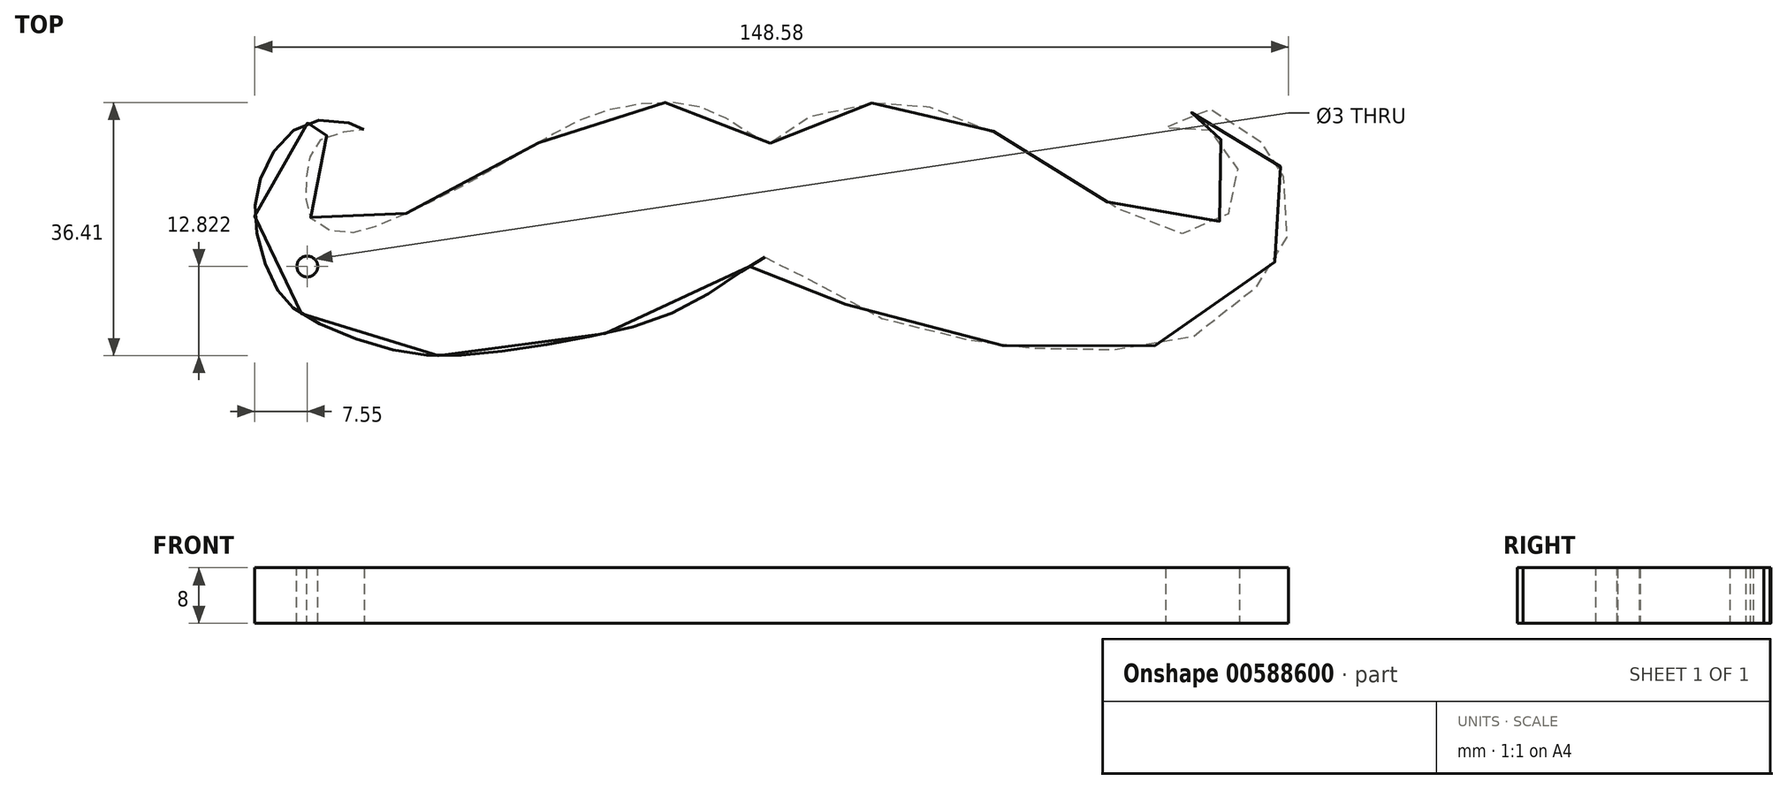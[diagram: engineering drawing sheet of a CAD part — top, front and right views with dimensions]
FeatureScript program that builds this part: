
annotation { "Feature Type Name" : "Feature", "Feature Type Description" : "" }
export const myFeature = defineFeature(function(context is Context, id is Id, definition is map)
    precondition{}
    {
        {
            var Q0;
            Q0=qCreatedBy(makeId("Top.planeOp"),FACE);
            var sketch = newSketch(context, id + "F0", { "sketchPlane" : qUnion([Q0])});
            skPoint(sketch, "E0.41.internal.snap0", {"position": v(0, 19.04) * mm});
            skPoint(sketch, "E0.42.internal.snap0", {"position": v(0, 19.04) * mm});
            skFitSpline(sketch, "E0", {"points": [v(-75.65, 31.5) * mm, v(-81.55, 34.82) * mm, v(-89.12, 37.31) * mm, v(-100.1, 35.93) * mm, v(-108.77, 31.69) * mm, v(-120.85, 24.86) * mm, v(-130.81, 20.15) * mm, v(-136.63, 18.59) * mm, v(-141.52, 20.52) * mm, v(-142.35, 24.86) * mm, v(-141.8, 29.56) * mm, v(-138.84, 32.8) * mm, v(-134.04, 33.53) * mm, v(-138.38, 34.82) * mm, v(-144.93, 32.8) * mm, v(-149.08, 25.87) * mm, v(-149.54, 19.14) * mm, v(-146.77, 10.93) * mm, v(-142.9, 6.87) * mm, v(-130.72, 1.98) * mm, v(-119.84, 1.06) * mm, v(-102.4, 3.55) * mm, v(-87.09, 8.35) * mm, v(-76.85, 14.9) * mm, v(-74.45, 15.08) * mm, v(-66.51, 9.27) * mm, v(-48.25, 3.46) * mm, v(-39.58, 2.16) * mm, v(-25.37, 1.89) * mm, v(-11.62, 5.4) * mm, v(-2.95, 14.71) * mm, v(-1.19, 19.62) * mm, v(-2.02, 27.42) * mm, v(-2.57, 28.46) * mm, v(-7.96, 34.54) * mm, v(-14.66, 36.06) * mm, v(-18.81, 33.78) * mm, v(-15.42, 34.4) * mm, v(-10.3, 31.36) * mm, v(-8.37, 27.22) * mm, v(-9, 22.45) * mm, v(-13.49, 19.04) * mm, v(-19.57, 19.04) * mm, v(-30.77, 25.35) * mm, v(-37.26, 29.36) * mm, v(-49.7, 36) * mm, v(-57.72, 37.03) * mm, v(-64.56, 37.03) * mm, v(-73.96, 32.95) * mm, v(-75.65, 31.5) * mm]});
            skSolve(sketch);
        }
        {
            var Q0;
            Q0 = qSketchRegion(id + "F0", true);
            extrude(context, id + "F1", {"entities" : qUnion([Q0]), "depth" : 8 * mm, "offsetDistance" : 25 * mm});
        }
        {
            var Q0;
            Q0=makeQuery(id+"F1.opExtrude","CAP_FACE",FACE,{"disambiguationData":[OSD([sQuery(id+"F0.wireOp",EDGE,"E0")])],"isStart":false});
            var sketch = newSketch(context, id + "F2", { "sketchPlane" : qUnion([Q0])});
            skPoint(sketch, "E1", {"position": v(-142.2, 13.78) * mm});
            skSolve(sketch);
        }
        {
            var Q0;
            Q0=sQuery(id+"F2.wireOp",VERTEX,"E1");
            var Q1;
            Q1=makeQuery(id+"F1.opExtrude","SWEPT_BODY",BODY,{"disambiguationData":[OSD([sQuery(id+"F0.wireOp",EDGE,"E0")])]});
            hole(context, id + "F3", {"style" : HoleStyle.SIMPLE, "endStyle" : HoleEndStyle.THROUGH, "holeDiameter" : 3 * mm, "majorDiameter" : 5 * mm, "isTappedThrough" : true, "tappedDepth" : 12 * mm, "tapClearance" : 3, "locations" : qUnion([Q0]), "scope" : qUnion([Q1])});
        }
    });
